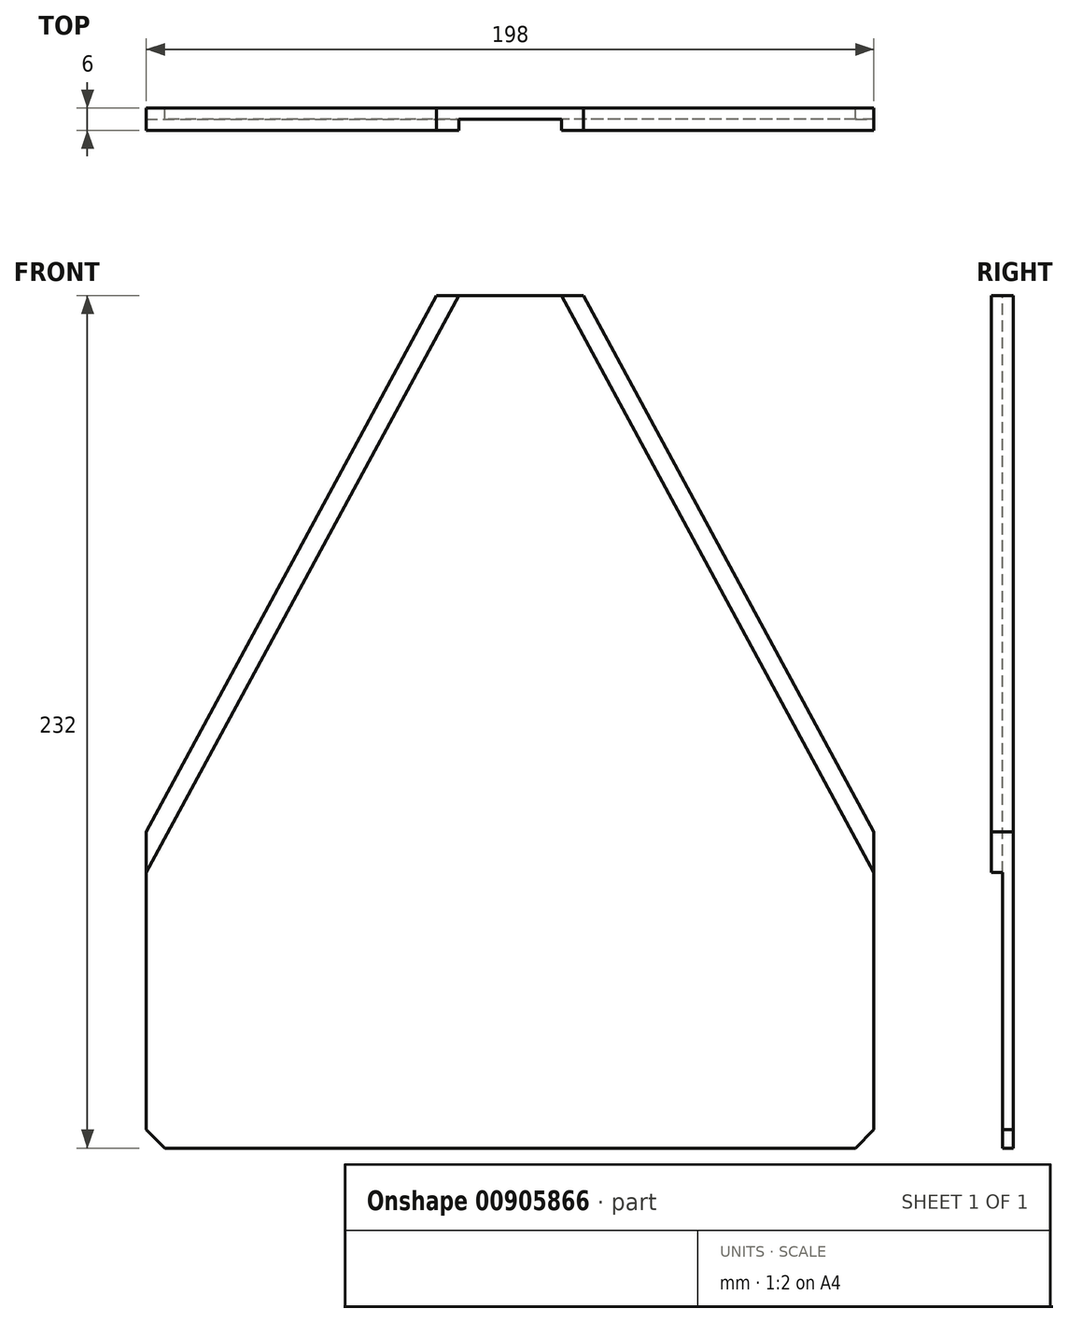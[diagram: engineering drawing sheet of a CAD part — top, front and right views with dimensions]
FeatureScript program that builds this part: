
annotation { "Feature Type Name" : "Feature", "Feature Type Description" : "" }
export const myFeature = defineFeature(function(context is Context, id is Id, definition is map)
    precondition{}
    {
        {
            var Q0;
            Q0=qCreatedBy(makeId("Front.planeOp"),FACE);
            var sketch = newSketch(context, id + "F0", { "sketchPlane" : qUnion([Q0])});
            skLineSegment(sketch, "E0.bottom", {"start": v(20, 116) * mm, "end": v(-20, 116) * mm});
            skLineSegment(sketch, "E0.top", {"start": v(94, -116) * mm, "end": v(-94, -116) * mm});
            skLineSegment(sketch, "E0.left", {"start": v(99, -30) * mm, "end": v(99, -111) * mm});
            skLineSegment(sketch, "E0.right", {"start": v(-99, -30) * mm, "end": v(-99, -111) * mm});
            skPoint(sketch, "E0.middle", {"position": v(0, 0) * mm});
            skLineSegment(sketch, "E1", {"start": v(99, -30) * mm, "end": v(99, -36) * mm});
            skLineSegment(sketch, "E2", {"start": v(0, 116) * mm, "end": v(-20, 116) * mm});
            skLineSegment(sketch, "E3", {"start": v(-20, 116) * mm, "end": v(20, 116) * mm});
            skLineSegment(sketch, "E4", {"start": v(-99, -111) * mm, "end": v(-99, -30) * mm});
            skLineSegment(sketch, "E5", {"start": v(-99, -30) * mm, "end": v(-20, 116) * mm});
            skPoint(sketch, "E6.orphan", {"position": v(-99, 116) * mm});
            skLineSegment(sketch, "E7", {"start": v(99, -111) * mm, "end": v(99, -30) * mm});
            skLineSegment(sketch, "E8", {"start": v(20, 116) * mm, "end": v(99, -30) * mm});
            skPoint(sketch, "E9.orphan", {"position": v(99, 116) * mm});
            skLineSegment(sketch, "E10.top", {"start": v(-99, -111) * mm, "end": v(-94, -111) * mm});
            skLineSegment(sketch, "E10.right", {"start": v(-94, -116) * mm, "end": v(-94, -111) * mm});
            skLineSegment(sketch, "E11", {"start": v(-99, -111) * mm, "end": v(-94, -116) * mm});
            skPoint(sketch, "E12.orphan", {"position": v(-99, -116) * mm});
            skLineSegment(sketch, "E13.top", {"start": v(99, -111) * mm, "end": v(94, -111) * mm});
            skLineSegment(sketch, "E13.right", {"start": v(94, -116) * mm, "end": v(94, -111) * mm});
            skLineSegment(sketch, "E14", {"start": v(94, -116) * mm, "end": v(99, -111) * mm});
            skPoint(sketch, "E15.orphan", {"position": v(99, -116) * mm});
            skLineSegment(sketch, "E16", {"start": v(99, -116) * mm, "end": v(99, -36) * mm});
            skLineSegment(sketch, "E17", {"start": v(-99, -116) * mm, "end": v(-99, -36) * mm});
            skLineSegment(sketch, "E18", {"start": v(-99, -36) * mm, "end": v(-99, -116) * mm});
            skLineSegment(sketch, "E19", {"start": v(0, 116) * mm, "end": v(-14, 116) * mm});
            skLineSegment(sketch, "E20", {"start": v(-14, 116) * mm, "end": v(14, 116) * mm});
            skLineSegment(sketch, "E21", {"start": v(-14, 116) * mm, "end": v(-99, -36) * mm});
            skLineSegment(sketch, "E22", {"start": v(14, 116) * mm, "end": v(99, -36) * mm});
            skLineSegment(sketch, "E23", {"start": v(0, -116) * mm, "end": v(0, 116) * mm});
            skSolve(sketch);
        }
        {
            var Q0;
            Q0 = qSketchRegion(id + "F0", true);
            extrude(context, id + "F1", {"entities" : qUnion([Q0]), "depth" : 3 * mm, "offsetDistance" : 25 * mm});
        }
        {
            var Q0;
            Q0=makeQuery(id+"F1.opExtrude","CAP_FACE",FACE,{"disambiguationData":[OSD([sQuery(id+"F0.wireOp",EDGE,"E0.top"),sQuery(id+"F0.wireOp",EDGE,"E3"),sQuery(id+"F0.wireOp",EDGE,"E4"),sQuery(id+"F0.wireOp",EDGE,"E5"),sQuery(id+"F0.wireOp",EDGE,"E7"),sQuery(id+"F0.wireOp",EDGE,"E8"),sQuery(id+"F0.wireOp",EDGE,"E11"),sQuery(id+"F0.wireOp",EDGE,"E14"),sQuery(id+"F0.wireOp",EDGE,"E16"),sQuery(id+"F0.wireOp",EDGE,"E18"),sQuery(id+"F0.wireOp",EDGE,"E20")])],"isStart":false});
            var sketch = newSketch(context, id + "F2", { "sketchPlane" : qUnion([Q0])});
            skLineSegment(sketch, "E24", {"start": v(0, 116) * mm, "end": v(-14, 116) * mm});
            skLineSegment(sketch, "E25", {"start": v(-14, 116) * mm, "end": v(14, 116) * mm});
            skLineSegment(sketch, "E26", {"start": v(-99, -116) * mm, "end": v(-99, -36) * mm});
            skLineSegment(sketch, "E27", {"start": v(99, -36) * mm, "end": v(99, -116) * mm});
            skLineSegment(sketch, "E28", {"start": v(99, -30) * mm, "end": v(99, -41) * mm});
            skLineSegment(sketch, "E29", {"start": v(-99, -30) * mm, "end": v(-99, -41) * mm});
            skLineSegment(sketch, "E30", {"start": v(-99, -41) * mm, "end": v(-14, 116) * mm});
            skLineSegment(sketch, "E31", {"start": v(99, -41) * mm, "end": v(14, 116) * mm});
            skSolve(sketch);
        }
        {
            var Q0;
            {var subQ2=sQuery(id+"F2.wireOp",EDGE,"E30");Q0=makeQuery(id+"F2.imprint","IMPRINT",FACE,{"disambiguationData":[TD([[makeQuery(id+"F2.imprint","IMPRINT",EDGE,{"derivedFrom":subQ2}),1.0]])]});}
            var Q1;
            {var subQ2=sQuery(id+"F2.wireOp",EDGE,"E31");Q1=makeQuery(id+"F2.imprint","IMPRINT",FACE,{"disambiguationData":[TD([[makeQuery(id+"F2.imprint","IMPRINT",EDGE,{"derivedFrom":subQ2}),-1.0]])]});}
            extrude(context, id + "F3", {"entities" : qUnion([Q0, Q1]), "operationType" : NewBodyOperationType.ADD, "depth" : 3 * mm, "offsetDistance" : 25 * mm});
        }
    });
